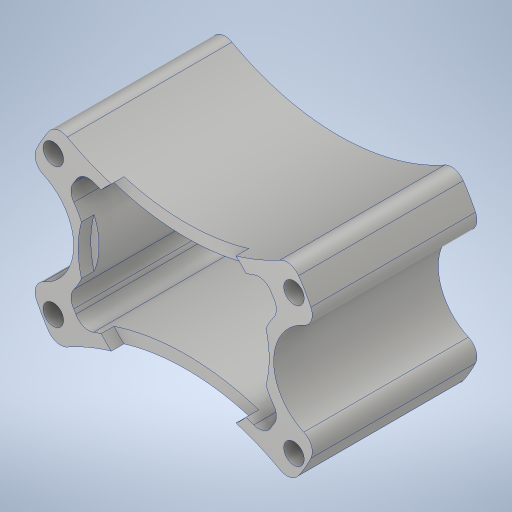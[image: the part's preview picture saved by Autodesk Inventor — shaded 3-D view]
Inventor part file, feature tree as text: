
AUTODESK INVENTOR PART (.ipt)
format: ipt  version: 2023.4 (Build 274418000, 418)  size: 364,544 bytes
history: native  units: in
note: dims shown in document units (in); Inventor stores cm internally (conversion verified against a paired STEP export)
features: sketch x2, extrude x2, fillet x1, hole x1
ambient origin geometry x8: Origin, YZ Plane, XZ Plane, XY Plane, X Axis, Y Axis, Z Axis, Center Point
bodies: Solid1 (feature_tree)
feature tree (6):
  sketch  "Sketch1"  dims[d0=2.375in d1=1.375in d2=0.5in]
  extrude  "Extrusion1"  Depth=0.5in
  fillet  "Fillet1"  Radius=0.5in
  hole  "Hole1"  [1 undecoded]
  extrude  "Extrusion2"  Depth=0.5in
  sketch  "Sketch3"  dims[d3=0.5in d4=0.5in d5=0.5in d6=1.25in d7=0.5in d8=0.5in d9=0.125in d10=0.125in d11=1.625in d12=0.0in d13=0.14in d14=0.201in d15=0.75in d16=0.385in d17=0.25in d18=0.5635in d19=1.0in d20=0.8108in d21=1.885in d22=0.125in d23=0.0in d24=0.125in d25=0.125in d26=0.125in d27=3.0in d28=1.0in]
note: 1 required parameter value undecoded (feature->parameter linkage not recoverable at this tier; creation-order binding heuristic only, values carry confidence <= 0.55)
